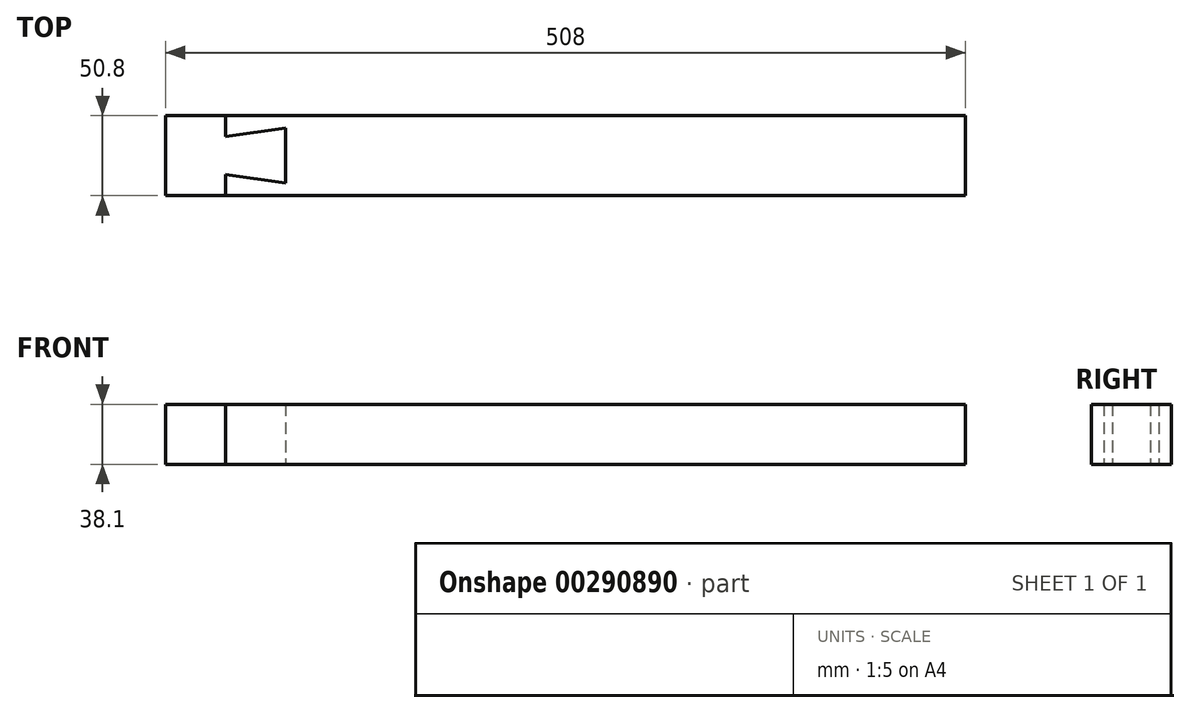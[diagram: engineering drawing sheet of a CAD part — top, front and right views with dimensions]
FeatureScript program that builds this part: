
annotation { "Feature Type Name" : "Feature", "Feature Type Description" : "" }
export const myFeature = defineFeature(function(context is Context, id is Id, definition is map)
    precondition{}
    {
        {
            var Q0;
            Q0=qCreatedBy(makeId("Top.planeOp"),FACE);
            var sketch = newSketch(context, id + "F0", { "sketchPlane" : qUnion([Q0])});
            skLineSegment(sketch, "E0.bottom", {"start": v(-254, 25.4) * mm, "end": v(254, 25.4) * mm});
            skLineSegment(sketch, "E0.top", {"start": v(-254, -25.4) * mm, "end": v(254, -25.4) * mm});
            skLineSegment(sketch, "E0.left", {"start": v(-254, 25.4) * mm, "end": v(-254, -25.4) * mm});
            skLineSegment(sketch, "E0.right", {"start": v(254, 25.4) * mm, "end": v(254, -25.4) * mm});
            skLineSegment(sketch, "E1", {"start": v(-215.9, 25.4) * mm, "end": v(-215.9, -25.4) * mm, "construction": true});
            skPoint(sketch, "E2", {"position": v(-254, 0) * mm});
            skLineSegment(sketch, "E3", {"start": v(-254, 0) * mm, "end": v(254, 0) * mm, "construction": true});
            skLineSegment(sketch, "E4", {"start": v(-215.9, 12.1) * mm, "end": v(-177.8, 17.46) * mm});
            skLineSegment(sketch, "E5", {"start": v(-177.8, 17.46) * mm, "end": v(-177.8, 0) * mm});
            skLineSegment(sketch, "E6.MirrorCS", {"start": v(-177.8, -17.46) * mm, "end": v(-177.8, 0) * mm});
            skLineSegment(sketch, "E7.MirrorCS", {"start": v(-215.9, -12.1) * mm, "end": v(-177.8, -17.46) * mm});
            skLineSegment(sketch, "E8", {"start": v(-177.8, -17.46) * mm, "end": v(-215.9, -17.46) * mm, "construction": true});
            skLineSegment(sketch, "E9", {"start": v(-215.9, 12.1) * mm, "end": v(-215.9, 25.4) * mm});
            skLineSegment(sketch, "E10", {"start": v(-215.9, -12.1) * mm, "end": v(-215.9, -25.4) * mm});
            skSolve(sketch);
        }
        {
            var Q0;
            Q0=qCreatedBy(makeId("Top.planeOp"),FACE);
            var sketch = newSketch(context, id + "F1", { "sketchPlane" : qUnion([Q0])});
            skLineSegment(sketch, "E11.0", {"start": v(-215.9, 12.1) * mm, "end": v(-215.9, 25.4) * mm});
            skLineSegment(sketch, "E12.0", {"start": v(-215.9, 12.1) * mm, "end": v(-177.8, 17.46) * mm});
            skLineSegment(sketch, "E13.0", {"start": v(-177.8, 17.46) * mm, "end": v(-177.8, 0) * mm});
            skLineSegment(sketch, "E14.0", {"start": v(-177.8, -17.46) * mm, "end": v(-177.8, 0) * mm});
            skLineSegment(sketch, "E15.0", {"start": v(-215.9, -12.1) * mm, "end": v(-177.8, -17.46) * mm});
            skLineSegment(sketch, "E16.0", {"start": v(-215.9, -12.1) * mm, "end": v(-215.9, -25.4) * mm});
            skLineSegment(sketch, "E17.0", {"start": v(-215.9, -25.4) * mm, "end": v(254, -25.4) * mm});
            skLineSegment(sketch, "E18.0", {"start": v(-215.9, 25.4) * mm, "end": v(254, 25.4) * mm});
            skLineSegment(sketch, "E19.0", {"start": v(254, 25.4) * mm, "end": v(254, -25.4) * mm});
            skSolve(sketch);
        }
        {
            var Q0;
            Q0=makeQuery(id+"F1.imprint","IMPRINT",FACE,{"disambiguationData":[TD([[makeQuery(id+"F1.imprint","IMPRINT",EDGE,{"derivedFrom":sQuery(id+"F1.wireOp",EDGE,"E11.0")}),-1.0]])]});
            extrude(context, id + "F2", {"entities" : qUnion([Q0]), "depth" : 38.1 * mm});
        }
        {
            var Q0;
            {var subQ0=sQuery(id+"F0.wireOp",EDGE,"E0.left");Q0=makeQuery(id+"F0.imprint","IMPRINT",FACE,{"disambiguationData":[TD([[makeQuery(id+"F0.imprint","IMPRINT",EDGE,{"derivedFrom":subQ0}),1.0]])]});}
            var Q1;
            Q1=makeQuery(id+"F2.opExtrude","CAP_FACE",FACE,{"disambiguationData":[OSD([sQuery(id+"F1.wireOp",EDGE,"E11.0"),sQuery(id+"F1.wireOp",EDGE,"E12.0"),sQuery(id+"F1.wireOp",EDGE,"E13.0"),sQuery(id+"F1.wireOp",EDGE,"E14.0"),sQuery(id+"F1.wireOp",EDGE,"E15.0"),sQuery(id+"F1.wireOp",EDGE,"E16.0"),sQuery(id+"F1.wireOp",EDGE,"E17.0"),sQuery(id+"F1.wireOp",EDGE,"E18.0"),sQuery(id+"F1.wireOp",EDGE,"E19.0")])],"isStart":false});
            extrude(context, id + "F3", {"entities" : qUnion([Q0]), "endBound" : BoundingType.UP_TO_SURFACE, "endBoundEntityFace" : qUnion([Q1]), "depth" : 25.4 * mm});
        }
    });
